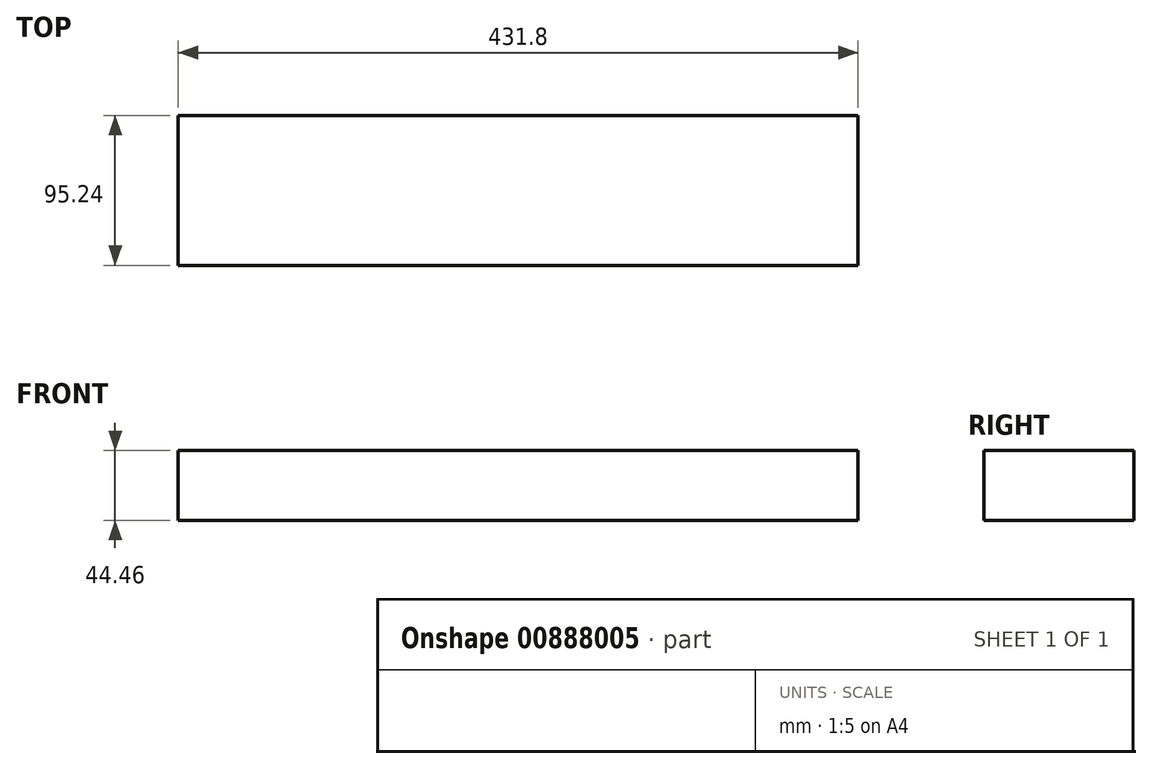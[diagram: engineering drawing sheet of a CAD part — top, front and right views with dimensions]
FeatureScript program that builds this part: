
annotation { "Feature Type Name" : "Feature", "Feature Type Description" : "" }
export const myFeature = defineFeature(function(context is Context, id is Id, definition is map)
    precondition{}
    {
        {
            var Q0;
            Q0=qCreatedBy(makeId("Right.planeOp"),FACE);
            var sketch = newSketch(context, id + "F0", { "sketchPlane" : qUnion([Q0])});
            skLineSegment(sketch, "E0.bottom", {"start": v(47.63, -22.22) * mm, "end": v(-47.62, -22.23) * mm});
            skLineSegment(sketch, "E0.top", {"start": v(47.63, 22.23) * mm, "end": v(-47.63, 22.22) * mm});
            skLineSegment(sketch, "E0.left", {"start": v(47.63, -22.22) * mm, "end": v(47.63, 22.23) * mm});
            skLineSegment(sketch, "E0.right", {"start": v(-47.63, -22.23) * mm, "end": v(-47.63, 22.23) * mm});
            skPoint(sketch, "E0.middle", {"position": v(0, 0) * mm});
            skSolve(sketch);
        }
        {
            var Q0;
            Q0=qSketchRegion(id+"F0",true);
            extrude(context, id + "F1", {"entities" : qUnion([Q0]), "endBound" : BoundingType.SYMMETRIC, "depth" : 431.8 * mm, "offsetDistance" : 25.4 * mm});
        }
    });
